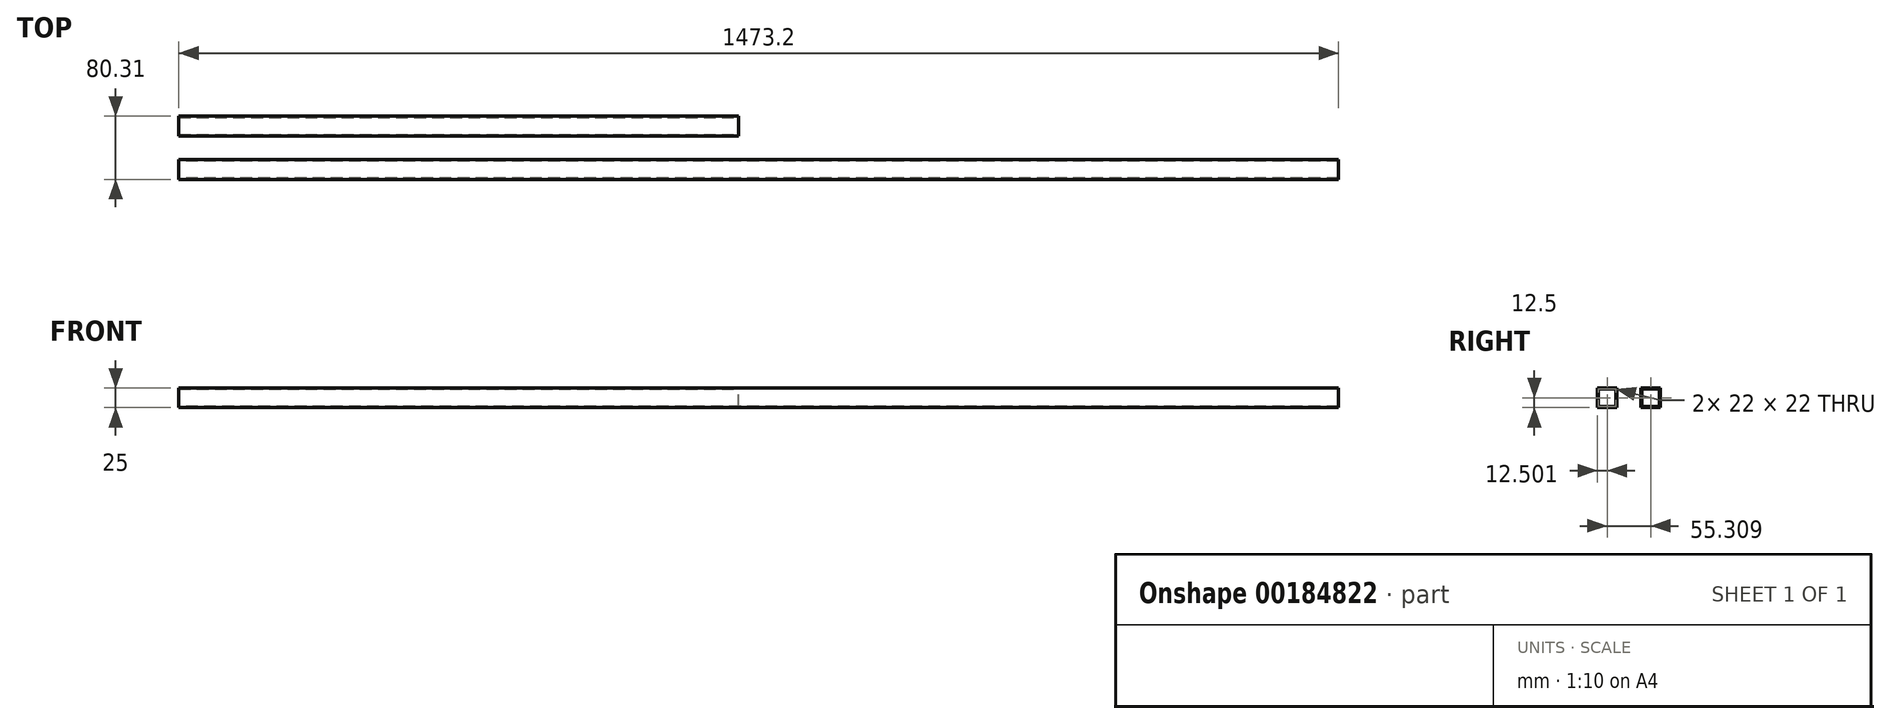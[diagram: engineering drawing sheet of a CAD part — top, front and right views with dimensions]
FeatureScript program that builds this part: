
annotation { "Feature Type Name" : "Feature", "Feature Type Description" : "" }
export const myFeature = defineFeature(function(context is Context, id is Id, definition is map)
    precondition{}
    {
        {
            var Q0;
            Q0=qCreatedBy(makeId("Right.planeOp"),FACE);
            var sketch = newSketch(context, id + "F0", { "sketchPlane" : qUnion([Q0])});
            skLineSegment(sketch, "E0.bottom", {"start": v(0, 0) * mm, "end": v(25, 0) * mm});
            skLineSegment(sketch, "E0.top", {"start": v(0, 25) * mm, "end": v(25, 25) * mm});
            skLineSegment(sketch, "E0.left", {"start": v(0, 0) * mm, "end": v(0, 25) * mm});
            skLineSegment(sketch, "E0.right", {"start": v(25, 0) * mm, "end": v(25, 25) * mm});
            skSolve(sketch);
        }
        {
            var Q0;
            Q0=makeQuery(id+"F0.imprint","IMPRINT",FACE,{"disambiguationData":[TD([[makeQuery(id+"F0.imprint","IMPRINT",EDGE,{"derivedFrom":sQuery(id+"F0.wireOp",EDGE,"E0.bottom")}),1.0]])]});
            extrude(context, id + "F1", {"entities" : qUnion([Q0]), "depth" : 711.2 * mm});
        }
        {
            var Q0;
            Q0=makeQuery(id+"F1.opExtrude","CAP_FACE",FACE,{"disambiguationData":[OSD([sQuery(id+"F0.wireOp",EDGE,"E0.bottom"),sQuery(id+"F0.wireOp",EDGE,"E0.top"),sQuery(id+"F0.wireOp",EDGE,"E0.left"),sQuery(id+"F0.wireOp",EDGE,"E0.right")])],"isStart":false});
            var sketch = newSketch(context, id + "F2", { "sketchPlane" : qUnion([Q0])});
            skLineSegment(sketch, "E1.bottom", {"start": v(1.5, 1.5) * mm, "end": v(23.5, 1.5) * mm});
            skLineSegment(sketch, "E1.top", {"start": v(1.5, 23.5) * mm, "end": v(23.5, 23.5) * mm});
            skLineSegment(sketch, "E1.left", {"start": v(1.5, 1.5) * mm, "end": v(1.5, 23.5) * mm});
            skLineSegment(sketch, "E1.right", {"start": v(23.5, 1.5) * mm, "end": v(23.5, 23.5) * mm});
            skSolve(sketch);
        }
        {
            var Q0;
            Q0=makeQuery(id+"F2.imprint","IMPRINT",FACE,{"disambiguationData":[TD([[makeQuery(id+"F2.imprint","IMPRINT",EDGE,{"derivedFrom":sQuery(id+"F2.wireOp",EDGE,"E1.bottom")}),1.0]])]});
            extrude(context, id + "F3", {"entities" : qUnion([Q0]), "operationType" : NewBodyOperationType.REMOVE, "endBound" : BoundingType.THROUGH_ALL, "oppositeDirection" : true, "depth" : 25 * mm});
        }
        {
            var Q0;
            Q0=makeQuery(id+"F1.opExtrude","SWEPT_BODY",BODY,{"disambiguationData":[OSD([sQuery(id+"F0.wireOp",EDGE,"E0.bottom"),sQuery(id+"F0.wireOp",EDGE,"E0.top"),sQuery(id+"F0.wireOp",EDGE,"E0.left"),sQuery(id+"F0.wireOp",EDGE,"E0.right")])]});
            transform(context, id + "F4", {"entities" : qUnion([Q0]), "transformType" : TransformType.TRANSLATION_3D, "dx" : 0 * mm, "dy" : 100 * mm, "dz" : 0 * mm, "makeCopy" : true});
        }
        {
            var Q0;
            Q0=makeQuery(id+"F4.opPattern","COPY",BODY,{"derivedFrom":makeQuery(id+"F1.opExtrude","SWEPT_BODY",BODY,{"disambiguationData":[OSD([sQuery(id+"F0.wireOp",EDGE,"E0.bottom"),sQuery(id+"F0.wireOp",EDGE,"E0.top"),sQuery(id+"F0.wireOp",EDGE,"E0.left"),sQuery(id+"F0.wireOp",EDGE,"E0.right")])]}),"instanceName":"1"});
            deleteBodies(context, id + "F5", {"entities" : qUnion([Q0])});
        }
        {
            var Q0;
            Q0=qCreatedBy(makeId("Right.planeOp"),FACE);
            var sketch = newSketch(context, id + "F6", { "sketchPlane" : qUnion([Q0])});
            skLineSegment(sketch, "E2.bottom", {"start": v(-30.3, 0) * mm, "end": v(-55.3, 0) * mm});
            skLineSegment(sketch, "E2.top", {"start": v(-30.3, 25) * mm, "end": v(-55.3, 25) * mm});
            skLineSegment(sketch, "E2.left", {"start": v(-30.3, 0) * mm, "end": v(-30.3, 25) * mm});
            skLineSegment(sketch, "E2.right", {"start": v(-55.3, 0) * mm, "end": v(-55.3, 25) * mm});
            skSolve(sketch);
        }
        {
            var Q0;
            Q0=makeQuery(id+"F6.imprint","IMPRINT",FACE,{"disambiguationData":[TD([[makeQuery(id+"F6.imprint","IMPRINT",EDGE,{"derivedFrom":sQuery(id+"F6.wireOp",EDGE,"E2.bottom")}),-1.0]])]});
            extrude(context, id + "F7", {"entities" : qUnion([Q0]), "depth" : 1473.2 * mm});
        }
        {
            var Q0;
            Q0=makeQuery(id+"F7.opExtrude","CAP_FACE",FACE,{"disambiguationData":[OSD([sQuery(id+"F6.wireOp",EDGE,"E2.bottom"),sQuery(id+"F6.wireOp",EDGE,"E2.top"),sQuery(id+"F6.wireOp",EDGE,"E2.left"),sQuery(id+"F6.wireOp",EDGE,"E2.right")])],"isStart":true});
            var sketch = newSketch(context, id + "F8", { "sketchPlane" : qUnion([Q0])});
            skLineSegment(sketch, "E3.bottom", {"start": v(31.8, 23.5) * mm, "end": v(53.8, 23.5) * mm});
            skLineSegment(sketch, "E3.top", {"start": v(31.8, 1.5) * mm, "end": v(53.8, 1.5) * mm});
            skLineSegment(sketch, "E3.left", {"start": v(31.8, 23.5) * mm, "end": v(31.8, 1.5) * mm});
            skLineSegment(sketch, "E3.right", {"start": v(53.8, 23.5) * mm, "end": v(53.8, 1.5) * mm});
            skSolve(sketch);
        }
        {
            var Q0;
            Q0=makeQuery(id+"F8.imprint","IMPRINT",FACE,{"disambiguationData":[TD([[makeQuery(id+"F8.imprint","IMPRINT",EDGE,{"derivedFrom":sQuery(id+"F8.wireOp",EDGE,"E3.bottom")}),-1.0]])]});
            extrude(context, id + "F9", {"entities" : qUnion([Q0]), "operationType" : NewBodyOperationType.REMOVE, "endBound" : BoundingType.THROUGH_ALL, "oppositeDirection" : true, "depth" : 25 * mm});
        }
    });
